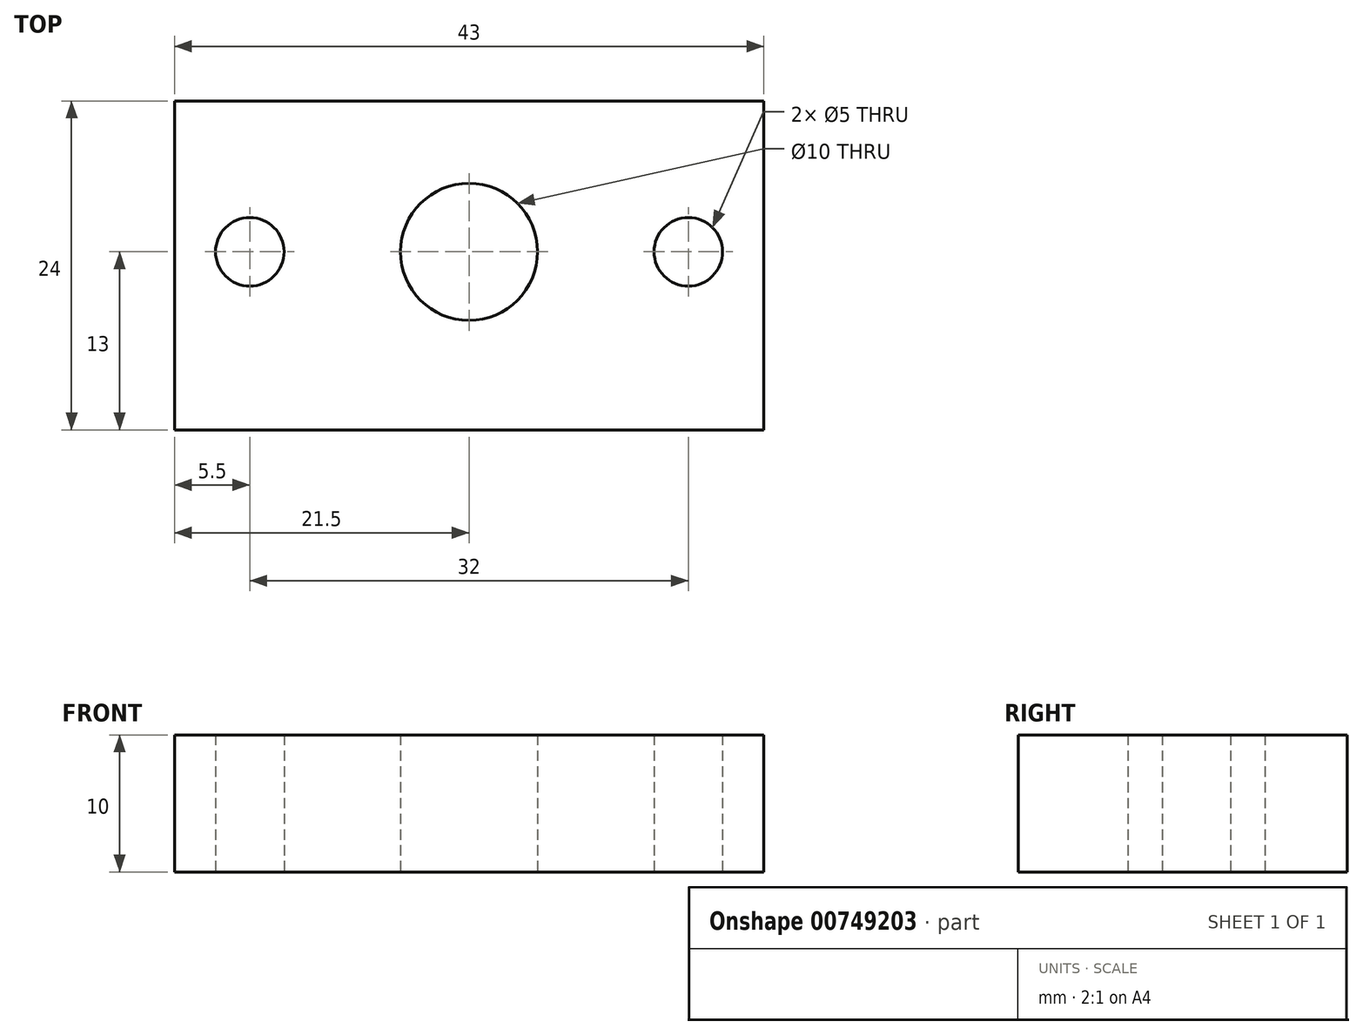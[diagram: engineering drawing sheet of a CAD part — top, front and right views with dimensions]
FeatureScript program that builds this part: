
annotation { "Feature Type Name" : "Feature", "Feature Type Description" : "" }
export const myFeature = defineFeature(function(context is Context, id is Id, definition is map)
    precondition{}
    {
        {
            var Q0;
            Q0=qCreatedBy(makeId("Top.planeOp"),FACE);
            var sketch = newSketch(context, id + "F0", { "sketchPlane" : qUnion([Q0])});
            skLineSegment(sketch, "E0.bottom", {"start": v(0, 0) * mm, "end": v(43, 0) * mm});
            skLineSegment(sketch, "E0.top", {"start": v(0, 24) * mm, "end": v(43, 24) * mm});
            skLineSegment(sketch, "E0.left", {"start": v(0, 0) * mm, "end": v(0, 24) * mm});
            skLineSegment(sketch, "E0.right", {"start": v(43, 0) * mm, "end": v(43, 24) * mm});
            skCircle(sketch, "E1", {"center": v(5.5, 13) * mm, "radius": 2.5 * mm});
            skCircle(sketch, "E2", {"center": v(37.5, 13) * mm, "radius": 2.5 * mm});
            skCircle(sketch, "E3", {"center": v(21.5, 13) * mm, "radius": 5 * mm});
            skSolve(sketch);
        }
        {
            var Q0;
            Q0=qSketchRegion(id+"F0",true);
            extrude(context, id + "F1", {"entities" : qUnion([Q0]), "depth" : 10 * mm});
        }
    });
